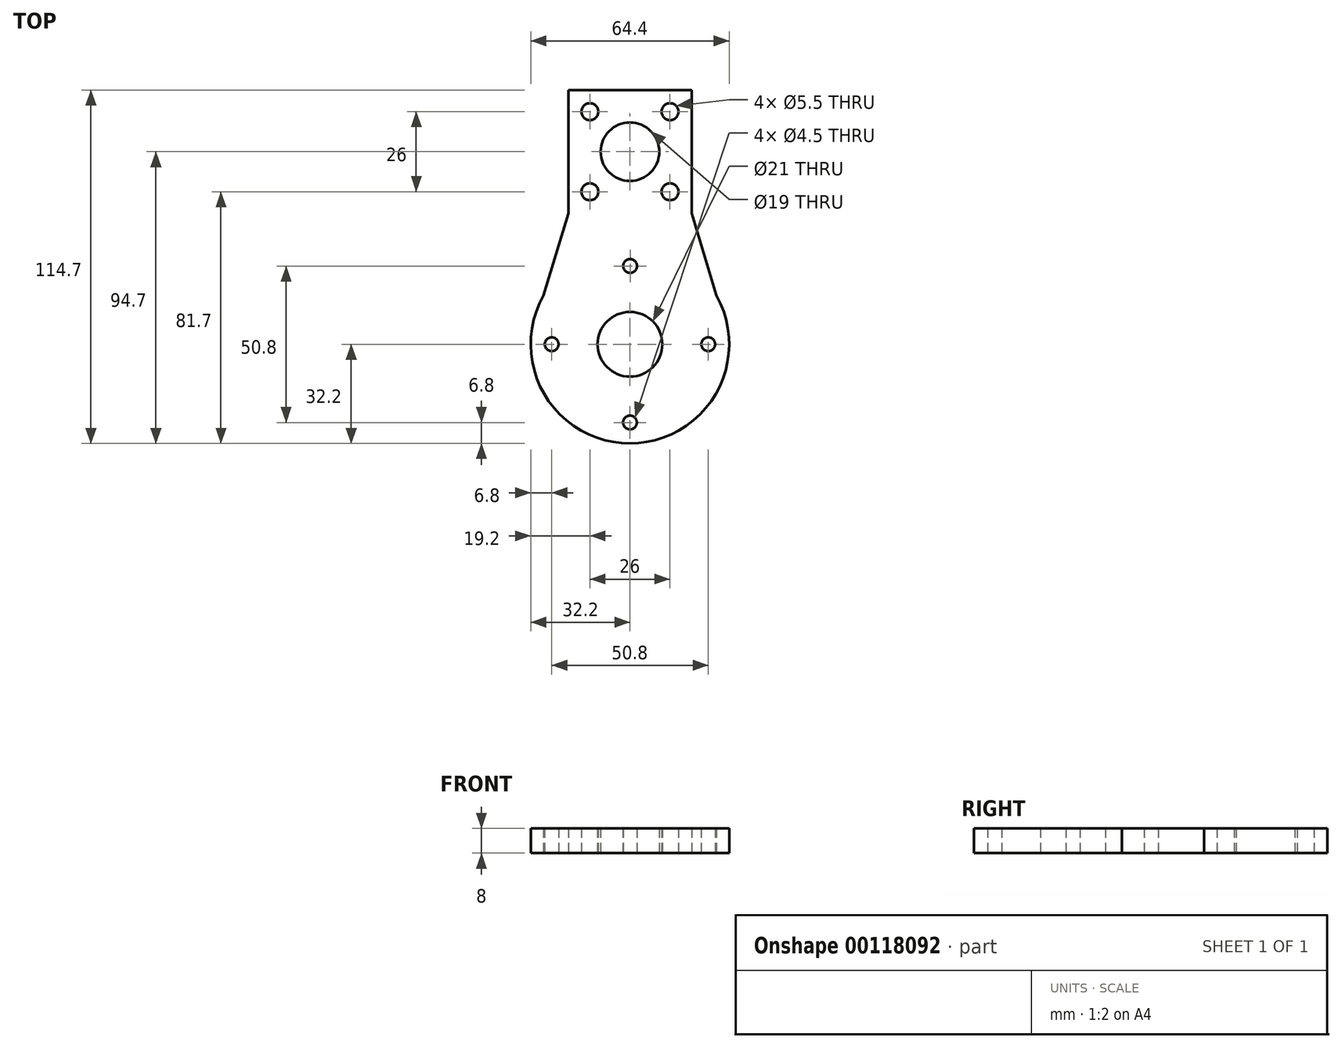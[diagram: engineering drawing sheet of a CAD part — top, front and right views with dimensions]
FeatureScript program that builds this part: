
annotation { "Feature Type Name" : "Feature", "Feature Type Description" : "" }
export const myFeature = defineFeature(function(context is Context, id is Id, definition is map)
    precondition{}
    {
        {
            var Q0;
            Q0=qCreatedBy(makeId("Top.planeOp"),FACE);
            var sketch = newSketch(context, id + "F0", { "sketchPlane" : qUnion([Q0])});
            skLineSegment(sketch, "E0.bottom", {"start": v(20, 20) * mm, "end": v(-20, 20) * mm});
            skLineSegment(sketch, "E0.left", {"start": v(20, 20) * mm, "end": v(20, -20) * mm});
            skLineSegment(sketch, "E0.right", {"start": v(-20, 20) * mm, "end": v(-20, -20) * mm});
            skPoint(sketch, "E0.middle", {"position": v(0, 0) * mm});
            skLineSegment(sketch, "E1", {"start": v(-20, -20) * mm, "end": v(20, -20) * mm, "construction": true});
            skLineSegment(sketch, "E2", {"start": v(-20, -20) * mm, "end": v(-20, -50) * mm, "construction": true});
            skLineSegment(sketch, "E3", {"start": v(-20, -50) * mm, "end": v(20, -50) * mm, "construction": true});
            skLineSegment(sketch, "E4", {"start": v(20, -50) * mm, "end": v(20, -20) * mm, "construction": true});
            skLineSegment(sketch, "E5", {"start": v(0, -50) * mm, "end": v(0, -30.3) * mm, "construction": true});
            skPoint(sketch, "E5.endSnap0", {"position": v(0, -50) * mm});
            skLineSegment(sketch, "E6", {"start": v(0, -50) * mm, "end": v(0, -62.5) * mm, "construction": true});
            skArc(sketch, "E7", {"start": v(-28.05, -46.68) * mm, "mid": v(0, -94.7) * mm, "end": v(28.05, -46.68) * mm});
            skLineSegment(sketch, "E8", {"start": v(-20, -20) * mm, "end": v(-28.05, -46.68) * mm});
            skLineSegment(sketch, "E9", {"start": v(20, -20) * mm, "end": v(28.05, -46.68) * mm});
            skCircle(sketch, "E10", {"center": v(0, -62.5) * mm, "radius": 10.5 * mm});
            skCircle(sketch, "E11", {"center": v(0, 0) * mm, "radius": 9.5 * mm});
            skLineSegment(sketch, "E12.bottom", {"start": v(13, 13) * mm, "end": v(-13, 13) * mm, "construction": true});
            skLineSegment(sketch, "E12.top", {"start": v(13, -13) * mm, "end": v(-13, -13) * mm, "construction": true});
            skLineSegment(sketch, "E12.left", {"start": v(13, 13) * mm, "end": v(13, -13) * mm, "construction": true});
            skLineSegment(sketch, "E12.right", {"start": v(-13, 13) * mm, "end": v(-13, -13) * mm, "construction": true});
            skCircle(sketch, "E13", {"center": v(-13, 13) * mm, "radius": 2.75 * mm});
            skCircle(sketch, "E14", {"center": v(13, 13) * mm, "radius": 2.75 * mm});
            skCircle(sketch, "E15", {"center": v(13, -13) * mm, "radius": 2.75 * mm});
            skCircle(sketch, "E16", {"center": v(-13, -13) * mm, "radius": 2.75 * mm});
            skCircle(sketch, "E17", {"center": v(0, -62.5) * mm, "radius": 25.4 * mm, "construction": true});
            skLineSegment(sketch, "E18", {"start": v(0, -62.5) * mm, "end": v(-25.4, -62.5) * mm, "construction": true});
            skLineSegment(sketch, "E19", {"start": v(0, -62.5) * mm, "end": v(0.05, -37.1) * mm, "construction": true});
            skLineSegment(sketch, "E20", {"start": v(0, -62.5) * mm, "end": v(25.4, -62.5) * mm, "construction": true});
            skLineSegment(sketch, "E21", {"start": v(0, -62.5) * mm, "end": v(0, -87.9) * mm, "construction": true});
            skCircle(sketch, "E22", {"center": v(-25.4, -62.5) * mm, "radius": 2.25 * mm});
            skCircle(sketch, "E23", {"center": v(0, -87.9) * mm, "radius": 2.25 * mm});
            skCircle(sketch, "E24", {"center": v(25.4, -62.5) * mm, "radius": 2.25 * mm});
            skCircle(sketch, "E25", {"center": v(0.05, -37.1) * mm, "radius": 2.25 * mm});
            skLineSegment(sketch, "E26", {"start": v(0, -30.3) * mm, "end": v(0, -20) * mm, "construction": true});
            skSolve(sketch);
        }
        {
            var Q0;
            Q0=makeQuery(id+"F0.imprint","IMPRINT",FACE,{"disambiguationData":[TD([[makeQuery(id+"F0.imprint","IMPRINT",EDGE,{"derivedFrom":sQuery(id+"F0.wireOp",EDGE,"E0.bottom")}),1.0]])]});
            extrude(context, id + "F1", {"entities" : qUnion([Q0]), "depth" : 8 * mm});
        }
    });
